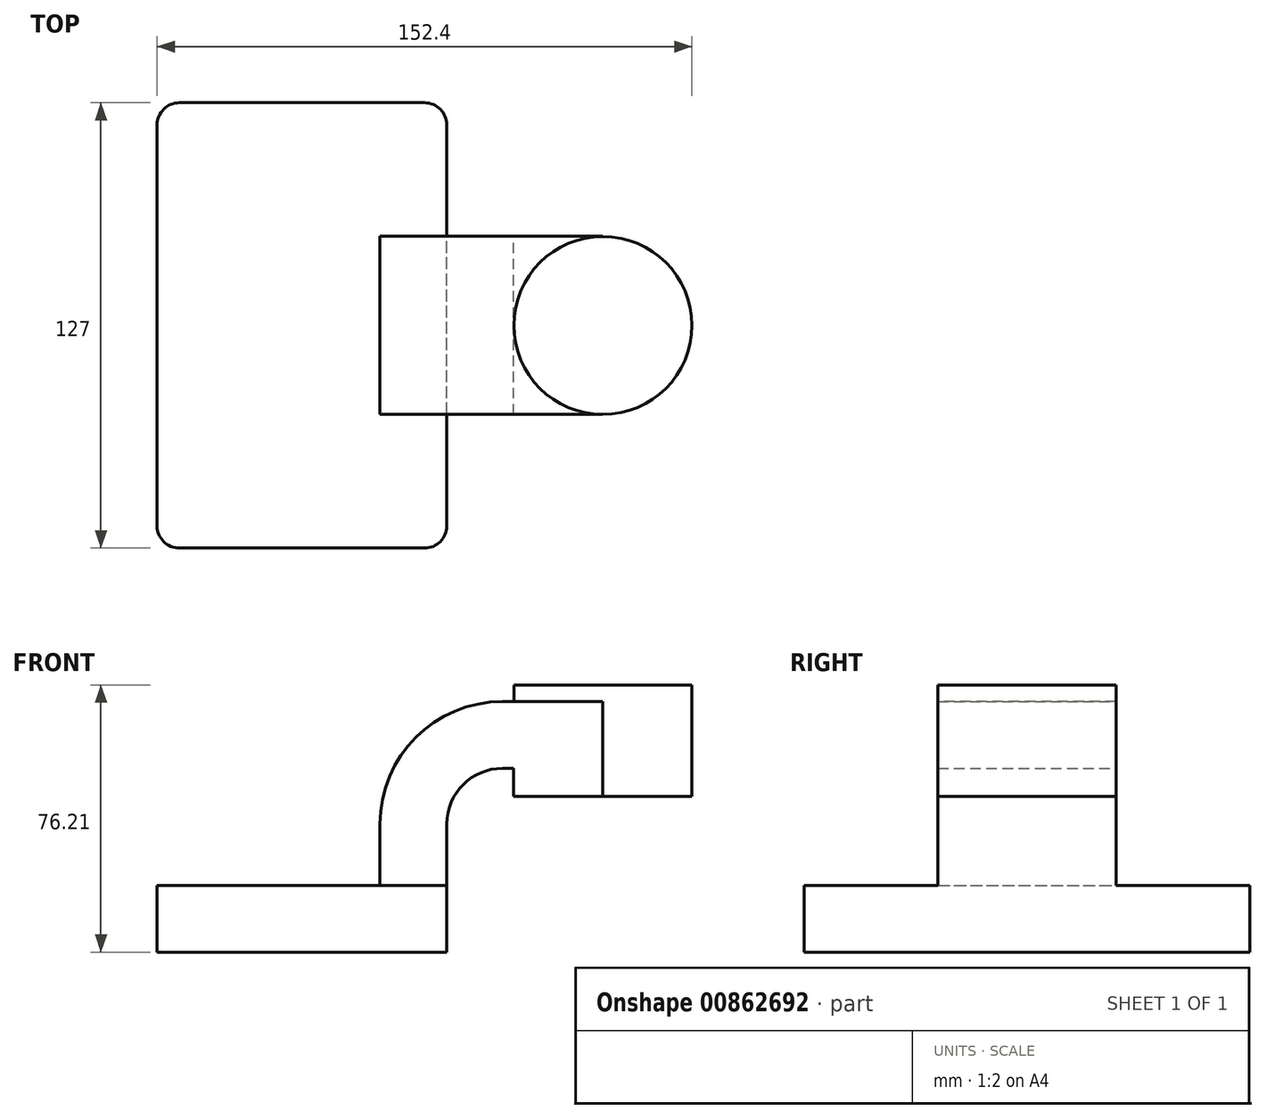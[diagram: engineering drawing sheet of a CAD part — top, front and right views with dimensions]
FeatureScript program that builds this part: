
annotation { "Feature Type Name" : "Feature", "Feature Type Description" : "" }
export const myFeature = defineFeature(function(context is Context, id is Id, definition is map)
    precondition{}
    {
        {
            var Q0;
            Q0=qCreatedBy(makeId("Front.planeOp"),FACE);
            var sketch = newSketch(context, id + "F0", { "sketchPlane" : qUnion([Q0])});
            skLineSegment(sketch, "E0.bottom", {"start": v(41.28, -9.52) * mm, "end": v(-41.27, -9.53) * mm});
            skLineSegment(sketch, "E0.top", {"start": v(41.28, 9.53) * mm, "end": v(-41.28, 9.53) * mm});
            skLineSegment(sketch, "E0.left", {"start": v(41.28, -9.52) * mm, "end": v(41.28, 9.53) * mm});
            skLineSegment(sketch, "E0.right", {"start": v(-41.28, -9.52) * mm, "end": v(-41.28, 9.53) * mm});
            skPoint(sketch, "E0.middle", {"position": v(0, 0) * mm});
            skLineSegment(sketch, "E1.bottom", {"start": v(111.13, 34.93) * mm, "end": v(60.33, 34.93) * mm});
            skLineSegment(sketch, "E1.top", {"start": v(111.13, 66.68) * mm, "end": v(60.33, 66.68) * mm});
            skLineSegment(sketch, "E1.left", {"start": v(111.13, 34.93) * mm, "end": v(111.13, 66.68) * mm});
            skLineSegment(sketch, "E1.right", {"start": v(60.33, 34.93) * mm, "end": v(60.33, 66.68) * mm});
            skPoint(sketch, "E1.middle", {"position": v(85.73, 50.8) * mm});
            skLineSegment(sketch, "E2", {"start": v(41.28, 9.53) * mm, "end": v(41.28, 27) * mm});
            skArc(sketch, "E3", {"start": v(41.28, 27) * mm, "mid": v(45.92, 38.23) * mm, "end": v(57.15, 42.88) * mm});
            skLineSegment(sketch, "E4", {"start": v(57.15, 42.88) * mm, "end": v(85.07, 42.88) * mm});
            skLineSegment(sketch, "E5.0", {"start": v(57.15, 61.93) * mm, "end": v(85.75, 61.93) * mm});
            skArc(sketch, "E5.1", {"start": v(22.23, 27) * mm, "mid": v(32.45, 51.7) * mm, "end": v(57.15, 61.93) * mm});
            skLineSegment(sketch, "E5.2", {"start": v(22.23, 9.53) * mm, "end": v(22.23, 27) * mm});
            skLineSegment(sketch, "E6", {"start": v(85.75, 66.68) * mm, "end": v(85.75, 34.93) * mm});
            skFitSpline(sketch, "E7", {"points": [v(-41.28, 9.52) * mm, v(57.15, 61.93) * mm], "startDerivative": vector(22.27, 106.96) * mm, "endDerivative": vector(122.54, -0.44) * mm});
            skSolve(sketch);
        }
        {
            var Q0;
            Q0=makeQuery(id+"F0.imprint","IMPRINT",FACE,{"disambiguationData":[TD([[makeQuery(id+"F0.imprint","IMPRINT",EDGE,{"derivedFrom":sQuery(id+"F0.wireOp",EDGE,"E0.bottom")}),-1.0]])]});
            extrude(context, id + "F1", {"entities" : qUnion([Q0]), "endBound" : BoundingType.SYMMETRIC, "depth" : 127 * mm, "offsetDistance" : 25.4 * mm});
        }
        {
            var Q0;
            {var subQ1=sQuery(id+"F0.wireOp",EDGE,"E2");Q0=makeQuery(id+"F0.imprint","IMPRINT",FACE,{"disambiguationData":[TD([[makeQuery(id+"F0.imprint","IMPRINT",EDGE,{"derivedFrom":subQ1}),1.0]])]});}
            var Q1;
            {var subQ0=sQuery(id+"F0.wireOp",EDGE,"E4");var subQ1=sQuery(id+"F0.wireOp",EDGE,"E1.right");var subQ2=makeQuery(id+"F0.imprint","INTERSECT",VERTEX,{"derivedFrom":[subQ1,subQ0]});Q1=makeQuery(id+"F0.imprint","IMPRINT",FACE,{"disambiguationData":[TD([[makeQuery(id+"F0.imprint","IMPRINT",EDGE,{"disambiguationData":[TD([[subQ2,-1.0]])],"derivedFrom":subQ1}),-1.0]])]});}
            extrude(context, id + "F2", {"entities" : qUnion([Q0, Q1]), "operationType" : NewBodyOperationType.ADD, "endBound" : BoundingType.SYMMETRIC, "depth" : 50.8 * mm, "offsetDistance" : 25.4 * mm});
        }
        {
            var Q0;
            Q0=makeQuery(id+"F0.imprint","IMPRINT",FACE,{"disambiguationData":[TD([[makeQuery(id+"F0.imprint","IMPRINT",EDGE,{"derivedFrom":sQuery(id+"F0.wireOp",EDGE,"E5.1")}),1.0]])]});
            extrude(context, id + "F3", {"entities" : qUnion([Q0]), "operationType" : NewBodyOperationType.ADD, "endBound" : BoundingType.SYMMETRIC, "depth" : 16.5 * mm, "offsetDistance" : 25.4 * mm});
        }
        {
            var Q0;
            {var subQ4=sQuery(id+"F0.wireOp",EDGE,"E1.left");Q0=makeQuery(id+"F0.imprint","IMPRINT",FACE,{"disambiguationData":[TD([[makeQuery(id+"F0.imprint","IMPRINT",EDGE,{"derivedFrom":subQ4}),1.0]])]});}
            var Q1;
            Q1=sQuery(id+"F0.wireOp",EDGE,"E6");
            revolve(context, id + "F4", {"operationType" : NewBodyOperationType.ADD, "surfaceOperationType" : NewSurfaceOperationType.NEW, "entities" : qUnion([Q0]), "axis" : qUnion([Q1]), "revolveType" : RevolveType.FULL});
        }
        {
            var Q0;
            Q0=makeQuery(id+"F1.opExtrude","CAP_EDGE",EDGE,{"disambiguationData":[OSD([sQuery(id+"F0.wireOp",EDGE,"E0.right")])],"isStart":false});
            var Q1;
            Q1=makeQuery(id+"F1.opExtrude","CAP_EDGE",EDGE,{"disambiguationData":[OSD([sQuery(id+"F0.wireOp",EDGE,"E0.left")])],"isStart":false});
            var Q2;
            Q2=makeQuery(id+"F1.opExtrude","CAP_EDGE",EDGE,{"disambiguationData":[OSD([sQuery(id+"F0.wireOp",EDGE,"E0.left")])],"isStart":true});
            var Q3;
            Q3=makeQuery(id+"F1.opExtrude","CAP_EDGE",EDGE,{"disambiguationData":[OSD([sQuery(id+"F0.wireOp",EDGE,"E0.right")])],"isStart":true});
            var Q4;
            Q4=makeQuery(id+"F3.opExtrude","CAP_EDGE",EDGE,{"disambiguationData":[OSD([sQuery(id+"F0.wireOp",EDGE,"E7")])],"isStart":true});
            var Q5;
            Q5=makeQuery(id+"F3.opExtrude","CAP_EDGE",EDGE,{"disambiguationData":[OSD([sQuery(id+"F0.wireOp",EDGE,"E7")])],"isStart":false});
            fillet(context, id + "F5", {"entities" : qUnion([Q0, Q1, Q2, Q3, Q4, Q5]), "radius" : 6.35 * mm, "tangentPropagation" : true, "allowEdgeOverflow" : false});
        }
    });
